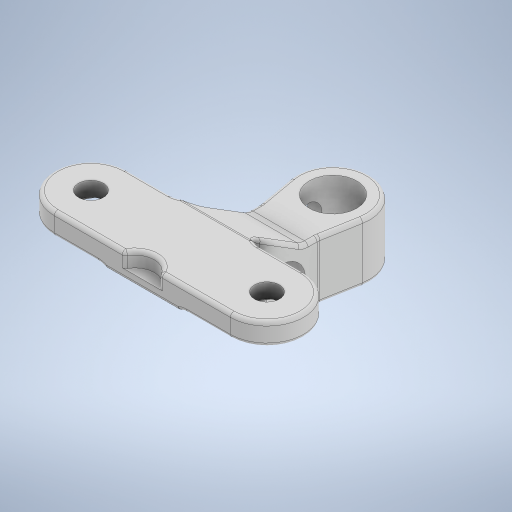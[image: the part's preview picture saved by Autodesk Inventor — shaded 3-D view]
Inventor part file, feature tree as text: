
AUTODESK INVENTOR PART (.ipt)
format: ipt  version: 2024.2 (Build 282272000, 272)  size: 532,992 bytes
history: native  units: mm
features: extrude x9, sketch x8, fillet x5, plane x3, projected_geometry x3
ambient origin geometry x8: Origin, YZ Plane, XZ Plane, XY Plane, X Axis, Y Axis, Z Axis, Center Point
bodies: Solid1 (feature_tree)
feature tree (28):
  extrude  "Extrusion1"  Depth=12.0mm
  extrude  "Extrusion2"  Depth=10.0mm
  sketch  "Sketch3"  dims[d5=3.0mm d6=0.0mm d7=5.7mm]
  extrude  "Extrusion3"  Depth=5.7mm
  extrude  "Extrusion4"  Depth=6.5mm
  plane  "Work Plane1"
  extrude  "Extrusion10"  Depth=8.0mm TaperAngle=0.0deg
  extrude  "Extrusion12"  Depth=6.0mm
  plane  "Work Plane5"
  extrude  "Extrusion13"  Depth=6.5mm
  plane  "Work Plane4"
  extrude  "Extrusion14"  Depth=10.0mm TaperAngle=0.0deg
  extrude  "Extrusion15"  Depth=2.8mm
  fillet  "Fillet14"  Radius=10.0mm
  fillet  "Fillet13"  Radius=2.0mm
  fillet  "Fillet15"  Radius=2.8mm
  fillet  "Fillet16"  Radius=10.0mm
  fillet  "Fillet17"  Radius=6.0mm
  sketch  "Sketch1"  dims[d0=24.0mm d1=12.0mm]
  sketch  "Sketch2"  dims[d2=3.4mm d4=10.0mm]
  sketch  "Sketch8"  dims[d8=1.0mm d9=0.0mm d10=6.5mm]
  sketch  "Sketch10"  dims[d11=10.0mm d13=8.0mm d14=0.0mm]
  projected_geometry  "Projected Loop3"
  sketch  "Sketch11"  dims[d15=8.0mm d16=0.0mm d17=6.0mm]
  sketch  "Sketch12"  dims[d41=10.0mm d42=6.5mm]
  sketch  "Sketch13"  dims[d44=8.0mm d45=0.0mm d49=10.0mm d50=0.0mm d51=2.8mm d52=10.0mm d53=0.0mm d54=2.0mm d55=2.8mm d56=10.0mm d57=0.0mm d61=6.0mm d62=5.25mm d63=2.0mm d64=0.0mm d66=2.0mm d67=6.0mm d68=10.0mm d69=6.0mm d74=2.0mm d75=0.5mm d76=0.5mm d77=0.5mm d78=0.5mm d28=0.0mm d29=0.0mm d30=0.0mm d31=0.0mm d32=0.0mm d39=0.0mm d40=0.0mm d73=0.0mm d79=0.0mm d80=0.0mm]
  projected_geometry  "Projected Loop4"
  projected_geometry  "Projected Loop5"
